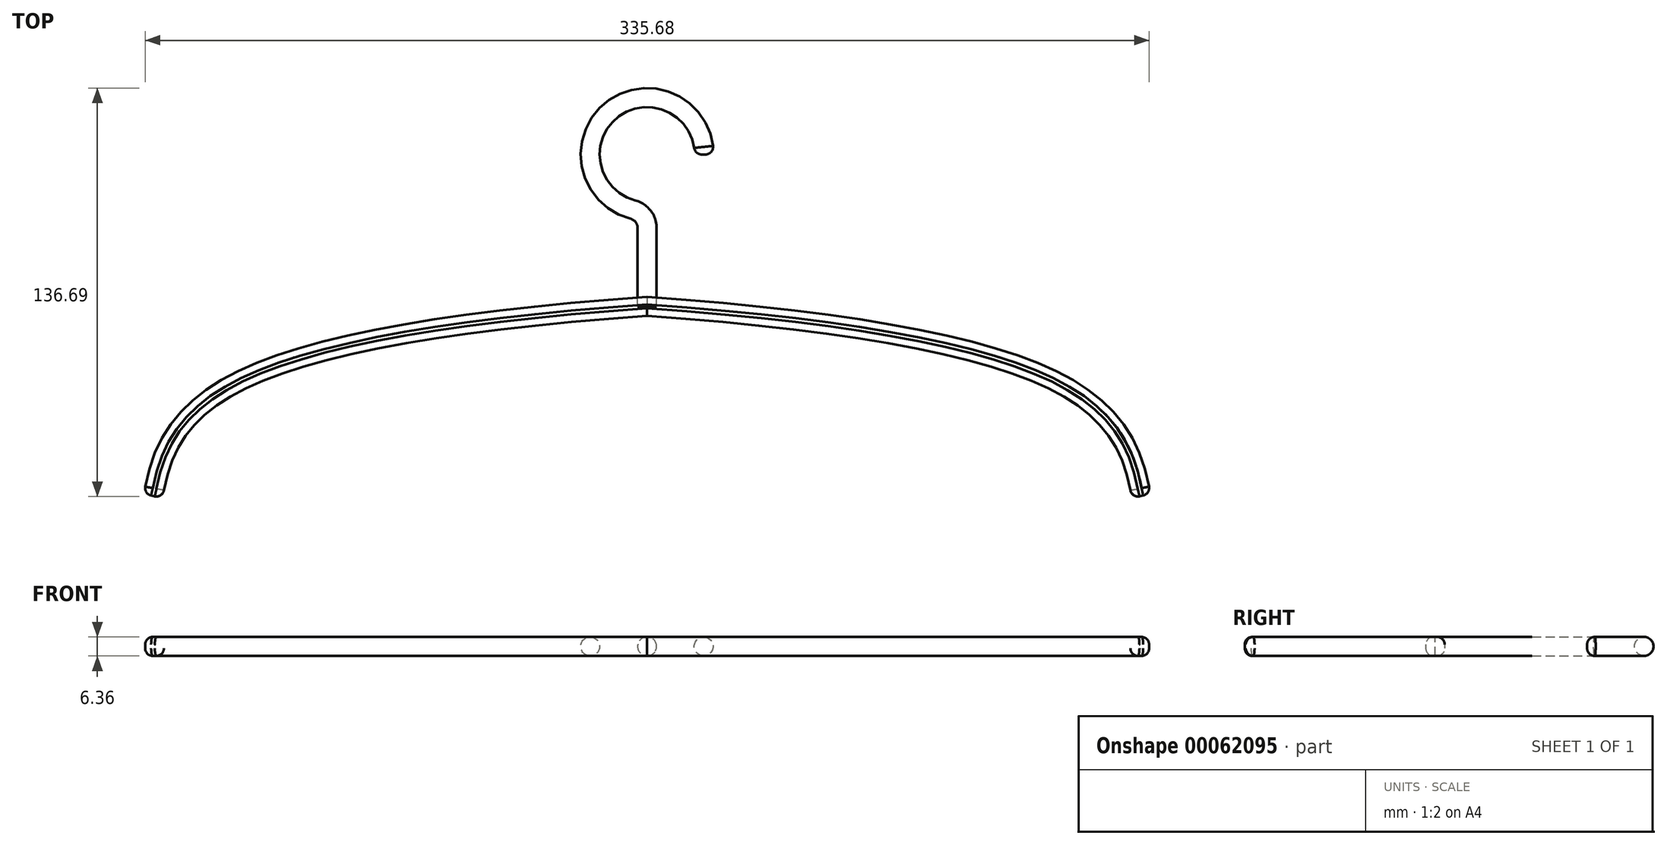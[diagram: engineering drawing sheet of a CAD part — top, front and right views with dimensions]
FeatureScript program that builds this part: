
annotation { "Feature Type Name" : "Feature", "Feature Type Description" : "" }
export const myFeature = defineFeature(function(context is Context, id is Id, definition is map)
    precondition{}
    {
        {
            var Q0;
            Q0=qCreatedBy(makeId("Top.planeOp"),FACE);
            var sketch = newSketch(context, id + "F0", { "sketchPlane" : qUnion([Q0])});
            skLineSegment(sketch, "E0", {"start": v(0, 0) * mm, "end": v(0, 26.2) * mm});
            skArc(sketch, "E1", {"start": v(19.05, 50.8) * mm, "mid": v(-11.67, 65.86) * mm, "end": v(-4.76, 32.35) * mm});
            skLineSegment(sketch, "E2", {"start": v(-165.1, 68.06) * mm, "end": v(-165.1, -63.5) * mm, "construction": true});
            skLineSegment(sketch, "E3", {"start": v(-165.1, -63.5) * mm, "end": v(0, -63.5) * mm, "construction": true});
            skFitSpline(sketch, "E4", {"points": [v(0, 0) * mm, v(-118, -17.83) * mm, v(-153.09, -36.92) * mm, v(-165.1, -63.5) * mm], "startDerivative": vector(-307.5, -22.13) * mm, "endDerivative": vector(-20.64, -141.72) * mm});
            skPoint(sketch, "E5.visualSharp", {"position": v(0, 31.75) * mm});
            skArc(sketch, "E5.filletArc", {"start": v(0, 26.2) * mm, "mid": v(-1.33, 30.1) * mm, "end": v(-4.76, 32.35) * mm});
            skSolve(sketch);
        }
        {
            var Q0;
            Q0=qCreatedBy(makeId("Right.planeOp"),FACE);
            var sketch = newSketch(context, id + "F1", { "sketchPlane" : qUnion([Q0])});
            skLineSegment(sketch, "E6.rect.bottom", {"start": v(0.63, 3.18) * mm, "end": v(-0.64, 3.18) * mm});
            skLineSegment(sketch, "E6.rect.top", {"start": v(0.63, -3.18) * mm, "end": v(-0.64, -3.18) * mm});
            skLineSegment(sketch, "E6.rect.left", {"start": v(3.18, 0.64) * mm, "end": v(3.18, -0.63) * mm});
            skLineSegment(sketch, "E6.rect.right", {"start": v(-3.18, 0.64) * mm, "end": v(-3.18, -0.64) * mm});
            skPoint(sketch, "E6.rect.middle", {"position": v(0, 0) * mm});
            skPoint(sketch, "E7.visualSharp", {"position": v(3.18, 3.18) * mm});
            skArc(sketch, "E7.filletArc", {"start": v(3.17, 0.64) * mm, "mid": v(2.43, 2.43) * mm, "end": v(0.63, 3.18) * mm});
            skPoint(sketch, "E8.visualSharp", {"position": v(3.18, -3.18) * mm});
            skArc(sketch, "E8.filletArc", {"start": v(0.63, -3.18) * mm, "mid": v(2.43, -2.43) * mm, "end": v(3.18, -0.63) * mm});
            skPoint(sketch, "E9.visualSharp", {"position": v(-3.18, 3.18) * mm});
            skArc(sketch, "E9.filletArc", {"start": v(-0.64, 3.18) * mm, "mid": v(-2.43, 2.43) * mm, "end": v(-3.18, 0.64) * mm});
            skPoint(sketch, "E10.visualSharp", {"position": v(-3.18, -3.18) * mm});
            skArc(sketch, "E10.filletArc", {"start": v(-3.18, -0.64) * mm, "mid": v(-2.43, -2.43) * mm, "end": v(-0.64, -3.18) * mm});
            skSolve(sketch);
        }
        {
            var Q0;
            Q0=makeQuery(id+"F1.imprint","IMPRINT",FACE,{"disambiguationData":[TD([[makeQuery(id+"F1.imprint","IMPRINT",EDGE,{"derivedFrom":sQuery(id+"F1.wireOp",EDGE,"E6.rect.bottom")}),1.0]])]});
            var Q1;
            Q1=sQuery(id+"F0.wireOp",EDGE,"E4");
            sweep(context, id + "F2", {"profiles" : qUnion([Q0]), "path" : qUnion([Q1])});
        }
        {
            var Q0;
            Q0=qCreatedBy(makeId("Front.planeOp"),FACE);
            var sketch = newSketch(context, id + "F3", { "sketchPlane" : qUnion([Q0])});
            skCircle(sketch, "E11", {"center": v(0, 0) * mm, "radius": 3.18 * mm});
            skSolve(sketch);
        }
        {
            var Q0;
            Q0=makeQuery(id+"F3.imprint","IMPRINT",FACE,{"disambiguationData":[TD([[makeQuery(id+"F3.imprint","IMPRINT",EDGE,{"derivedFrom":sQuery(id+"F3.wireOp",EDGE,"E11")}),1.0]])]});
            var Q1;
            Q1=sQuery(id+"F0.wireOp",EDGE,"E0");
            var Q2;
            Q2=sQuery(id+"F0.wireOp",EDGE,"E5.filletArc");
            var Q3;
            Q3=sQuery(id+"F0.wireOp",EDGE,"E1");
            sweep(context, id + "F4", {"profiles" : qUnion([Q0]), "path" : qUnion([Q1, Q2, Q3])});
        }
        {
            var Q0;
            Q0=makeQuery(id+"F2.opSweep","CAP_EDGE",EDGE,{"disambiguationData":[OSD([sQuery(id+"F0.wireOp",VERTEX,"E4.end"),sQuery(id+"F1.wireOp",EDGE,"E7.filletArc")])],"isStart":false});
            var Q1;
            Q1=makeQuery(id+"F2.opSweep","CAP_EDGE",EDGE,{"disambiguationData":[OSD([sQuery(id+"F0.wireOp",VERTEX,"E4.end"),sQuery(id+"F1.wireOp",EDGE,"E6.rect.left")])],"isStart":false});
            var Q2;
            Q2=makeQuery(id+"F2.opSweep","CAP_EDGE",EDGE,{"disambiguationData":[OSD([sQuery(id+"F0.wireOp",VERTEX,"E4.end"),sQuery(id+"F1.wireOp",EDGE,"E8.filletArc")])],"isStart":false});
            var Q3;
            Q3=makeQuery(id+"F2.opSweep","CAP_EDGE",EDGE,{"disambiguationData":[OSD([sQuery(id+"F0.wireOp",VERTEX,"E4.end"),sQuery(id+"F1.wireOp",EDGE,"E6.rect.top")])],"isStart":false});
            var Q4;
            Q4=makeQuery(id+"F2.opSweep","CAP_EDGE",EDGE,{"disambiguationData":[OSD([sQuery(id+"F0.wireOp",VERTEX,"E4.end"),sQuery(id+"F1.wireOp",EDGE,"E10.filletArc")])],"isStart":false});
            var Q5;
            Q5=makeQuery(id+"F2.opSweep","CAP_EDGE",EDGE,{"disambiguationData":[OSD([sQuery(id+"F0.wireOp",VERTEX,"E4.end"),sQuery(id+"F1.wireOp",EDGE,"E6.rect.right")])],"isStart":false});
            var Q6;
            Q6=makeQuery(id+"F2.opSweep","CAP_EDGE",EDGE,{"disambiguationData":[OSD([sQuery(id+"F0.wireOp",VERTEX,"E4.end"),sQuery(id+"F1.wireOp",EDGE,"E9.filletArc")])],"isStart":false});
            var Q7;
            Q7=makeQuery(id+"F2.opSweep","CAP_EDGE",EDGE,{"disambiguationData":[OSD([sQuery(id+"F0.wireOp",VERTEX,"E4.end"),sQuery(id+"F1.wireOp",EDGE,"E6.rect.bottom")])],"isStart":false});
            fillet(context, id + "F5", {"entities" : qUnion([Q0, Q1, Q2, Q3, Q4, Q5, Q6, Q7]), "radius" : 2.54 * mm, "tangentPropagation" : true, "allowEdgeOverflow" : false});
        }
        {
            var Q0;
            Q0=makeQuery(id+"F2.opSweep","SWEPT_BODY",BODY,{"disambiguationData":[OSD([sQuery(id+"F0.wireOp",EDGE,"E4"),sQuery(id+"F1.wireOp",EDGE,"E6.rect.bottom"),sQuery(id+"F1.wireOp",EDGE,"E6.rect.top"),sQuery(id+"F1.wireOp",EDGE,"E6.rect.left"),sQuery(id+"F1.wireOp",EDGE,"E6.rect.right"),sQuery(id+"F1.wireOp",EDGE,"E7.filletArc"),sQuery(id+"F1.wireOp",EDGE,"E8.filletArc"),sQuery(id+"F1.wireOp",EDGE,"E9.filletArc"),sQuery(id+"F1.wireOp",EDGE,"E10.filletArc")])]});
            var Q1;
            Q1=qCreatedBy(makeId("Right.planeOp"),FACE);
            mirror(context, id + "F6", {"entities" : qUnion([Q0]), "mirrorPlane" : qUnion([Q1])});
        }
        {
            var Q0;
            Q0=makeQuery(id+"F4.opSweep","CAP_EDGE",EDGE,{"disambiguationData":[OSD([sQuery(id+"F0.wireOp",VERTEX,"E1.start"),sQuery(id+"F3.wireOp",EDGE,"E11")])],"isStart":false});
            fillet(context, id + "F7", {"entities" : qUnion([Q0]), "radius" : 2.54 * mm, "tangentPropagation" : true, "allowEdgeOverflow" : false});
        }
    });
